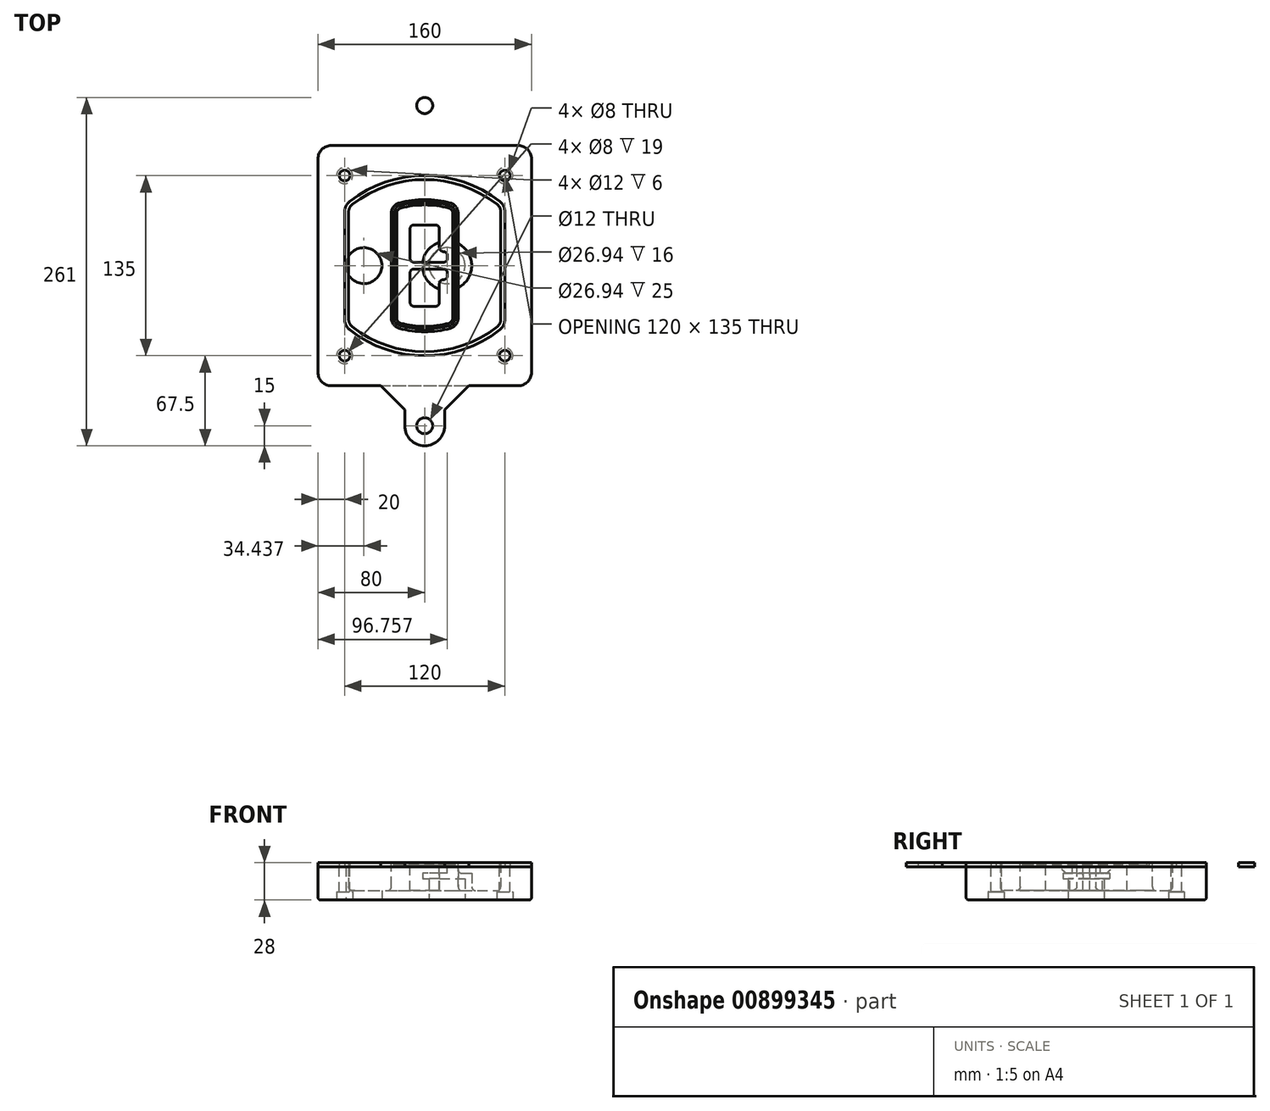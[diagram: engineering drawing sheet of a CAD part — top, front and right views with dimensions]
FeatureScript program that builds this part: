
annotation { "Feature Type Name" : "Feature", "Feature Type Description" : "" }
export const myFeature = defineFeature(function(context is Context, id is Id, definition is map)
    precondition{}
    {
        {
            var Q0;
            Q0=qCreatedBy(makeId("Top.planeOp"),FACE);
            var sketch = newSketch(context, id + "F0", { "sketchPlane" : qUnion([Q0])});
            skPoint(sketch, "E0.rect.middle", {"position": v(0, 0) * mm});
            skLineSegment(sketch, "E1.bottom", {"start": v(-70, -90) * mm, "end": v(70, -90) * mm});
            skLineSegment(sketch, "E1.top", {"start": v(-70, 90) * mm, "end": v(70, 90) * mm});
            skLineSegment(sketch, "E1.left", {"start": v(-80, -80) * mm, "end": v(-80, 80) * mm});
            skLineSegment(sketch, "E1.right", {"start": v(80, -80) * mm, "end": v(80, 80) * mm});
            skLineSegment(sketch, "E2", {"start": v(-80, 90) * mm, "end": v(80, -90) * mm, "construction": true});
            skLineSegment(sketch, "E3", {"start": v(80, 90) * mm, "end": v(-80, -90) * mm, "construction": true});
            skCircle(sketch, "E4", {"center": v(-60, 67.5) * mm, "radius": 4 * mm});
            skCircle(sketch, "E5", {"center": v(60, 67.5) * mm, "radius": 4 * mm});
            skCircle(sketch, "E6", {"center": v(60, -67.5) * mm, "radius": 4 * mm});
            skCircle(sketch, "E7", {"center": v(-60, -67.5) * mm, "radius": 4 * mm});
            skLineSegment(sketch, "E8", {"start": v(-60, 67.5) * mm, "end": v(60, 67.5) * mm, "construction": true});
            skLineSegment(sketch, "E9", {"start": v(60, 67.5) * mm, "end": v(60, -67.5) * mm, "construction": true});
            skLineSegment(sketch, "E10", {"start": v(60, -67.5) * mm, "end": v(-60, -67.5) * mm, "construction": true});
            skLineSegment(sketch, "E11", {"start": v(-60, -67.5) * mm, "end": v(-60, 67.5) * mm, "construction": true});
            skLineSegment(sketch, "E12", {"start": v(-60, 40.3) * mm, "end": v(-60, -40.3) * mm});
            skLineSegment(sketch, "E13", {"start": v(60, 40.3) * mm, "end": v(60, -40.3) * mm});
            skArc(sketch, "E14", {"start": v(56.15, 48.18) * mm, "mid": v(0, 67.5) * mm, "end": v(-56.15, 48.18) * mm});
            skArc(sketch, "E15", {"start": v(-56.15, -48.18) * mm, "mid": v(0, -67.5) * mm, "end": v(56.15, -48.18) * mm});
            skLineSegment(sketch, "E16", {"start": v(-60, 0) * mm, "end": v(60, 0) * mm, "construction": true});
            skPoint(sketch, "E17.visualSharp", {"position": v(-60, -45) * mm});
            skArc(sketch, "E17.filletArc", {"start": v(-60, -40.3) * mm, "mid": v(-58.99, -44.68) * mm, "end": v(-56.15, -48.18) * mm});
            skPoint(sketch, "E18.visualSharp", {"position": v(-60, 45) * mm});
            skArc(sketch, "E18.filletArc", {"start": v(-56.15, 48.18) * mm, "mid": v(-58.99, 44.68) * mm, "end": v(-60, 40.3) * mm});
            skPoint(sketch, "E19.visualSharp", {"position": v(60, 45) * mm});
            skArc(sketch, "E19.filletArc", {"start": v(60, 40.3) * mm, "mid": v(58.99, 44.68) * mm, "end": v(56.15, 48.18) * mm});
            skPoint(sketch, "E20.visualSharp", {"position": v(60, -45) * mm});
            skArc(sketch, "E20.filletArc", {"start": v(56.15, -48.18) * mm, "mid": v(58.99, -44.68) * mm, "end": v(60, -40.3) * mm});
            skPoint(sketch, "E21.visualSharp", {"position": v(-80, 90) * mm});
            skArc(sketch, "E21.filletArc", {"start": v(-70, 90) * mm, "mid": v(-77.07, 87.07) * mm, "end": v(-80, 80) * mm});
            skPoint(sketch, "E22.visualSharp", {"position": v(80, 90) * mm});
            skArc(sketch, "E22.filletArc", {"start": v(80, 80) * mm, "mid": v(77.07, 87.07) * mm, "end": v(70, 90) * mm});
            skPoint(sketch, "E23.visualSharp", {"position": v(80, -90) * mm});
            skArc(sketch, "E23.filletArc", {"start": v(70, -90) * mm, "mid": v(77.07, -87.07) * mm, "end": v(80, -80) * mm});
            skPoint(sketch, "E24.visualSharp", {"position": v(-80, -90) * mm});
            skArc(sketch, "E24.filletArc", {"start": v(-80, -80) * mm, "mid": v(-77.07, -87.07) * mm, "end": v(-70, -90) * mm});
            skArc(sketch, "E25.0", {"start": v(57, 40.3) * mm, "mid": v(56.3, 43.36) * mm, "end": v(54.3, 45.81) * mm});
            skLineSegment(sketch, "E25.1", {"start": v(57, 40.3) * mm, "end": v(57, -40.3) * mm});
            skArc(sketch, "E25.2", {"start": v(54.3, -45.81) * mm, "mid": v(56.3, -43.36) * mm, "end": v(57, -40.3) * mm});
            skArc(sketch, "E25.3", {"start": v(-54.3, -45.81) * mm, "mid": v(0, -64.5) * mm, "end": v(54.3, -45.81) * mm});
            skArc(sketch, "E25.4", {"start": v(-57, -40.3) * mm, "mid": v(-56.3, -43.36) * mm, "end": v(-54.3, -45.81) * mm});
            skArc(sketch, "E25.5", {"start": v(54.3, 45.81) * mm, "mid": v(0, 64.5) * mm, "end": v(-54.3, 45.81) * mm});
            skLineSegment(sketch, "E25.6", {"start": v(-57, 40.3) * mm, "end": v(-57, -40.3) * mm});
            skArc(sketch, "E25.7", {"start": v(-54.3, 45.81) * mm, "mid": v(-56.3, 43.36) * mm, "end": v(-57, 40.3) * mm});
            skArc(sketch, "E26.0", {"start": v(-58.62, 51.33) * mm, "mid": v(-62.58, 46.43) * mm, "end": v(-64, 40.3) * mm});
            skArc(sketch, "E26.1", {"start": v(58.62, 51.33) * mm, "mid": v(0, 71.5) * mm, "end": v(-58.62, 51.33) * mm});
            skArc(sketch, "E26.2", {"start": v(64, 40.3) * mm, "mid": v(62.58, 46.43) * mm, "end": v(58.62, 51.33) * mm});
            skLineSegment(sketch, "E26.3", {"start": v(64, 40.3) * mm, "end": v(64, -40.3) * mm});
            skArc(sketch, "E26.4", {"start": v(58.62, -51.33) * mm, "mid": v(62.58, -46.43) * mm, "end": v(64, -40.3) * mm});
            skLineSegment(sketch, "E26.5", {"start": v(-64, 40.3) * mm, "end": v(-64, -40.3) * mm});
            skArc(sketch, "E26.6", {"start": v(-58.62, -51.33) * mm, "mid": v(0, -71.5) * mm, "end": v(58.62, -51.33) * mm});
            skArc(sketch, "E26.7", {"start": v(-64, -40.3) * mm, "mid": v(-62.58, -46.43) * mm, "end": v(-58.62, -51.33) * mm});
            skSolve(sketch);
        }
        {
            var Q0;
            Q0=makeQuery(id+"F0.imprint","IMPRINT",FACE,{"disambiguationData":[TD([[makeQuery(id+"F0.imprint","IMPRINT",EDGE,{"derivedFrom":sQuery(id+"F0.wireOp",EDGE,"E1.bottom")}),1.0]])]});
            var Q1;
            Q1=makeQuery(id+"F0.imprint","IMPRINT",FACE,{"disambiguationData":[TD([[makeQuery(id+"F0.imprint","IMPRINT",EDGE,{"derivedFrom":sQuery(id+"F0.wireOp",EDGE,"E12")}),1.0]])]});
            var Q2;
            Q2=makeQuery(id+"F0.imprint","IMPRINT",FACE,{"disambiguationData":[TD([[makeQuery(id+"F0.imprint","IMPRINT",EDGE,{"derivedFrom":sQuery(id+"F0.wireOp",EDGE,"E25.0")}),1.0]])]});
            var Q3;
            Q3=makeQuery(id+"F0.imprint","IMPRINT",FACE,{"disambiguationData":[TD([[makeQuery(id+"F0.imprint","IMPRINT",EDGE,{"derivedFrom":sQuery(id+"F0.wireOp",EDGE,"E12")}),-1.0]])]});
            extrude(context, id + "F1", {"entities" : qUnion([Q0, Q1, Q2, Q3]), "oppositeDirection" : true, "depth" : 25 * mm});
        }
        {
            var Q0;
            Q0=makeQuery(id+"F0.imprint","IMPRINT",FACE,{"disambiguationData":[TD([[makeQuery(id+"F0.imprint","IMPRINT",EDGE,{"derivedFrom":sQuery(id+"F0.wireOp",EDGE,"E12")}),1.0]])]});
            extrude(context, id + "F2", {"entities" : qUnion([Q0]), "operationType" : NewBodyOperationType.ADD, "depth" : 3 * mm});
        }
        {
            var Q0;
            Q0=makeQuery(id+"F0.imprint","IMPRINT",FACE,{"disambiguationData":[TD([[makeQuery(id+"F0.imprint","IMPRINT",EDGE,{"derivedFrom":sQuery(id+"F0.wireOp",EDGE,"E25.0")}),1.0]])]});
            extrude(context, id + "F3", {"entities" : qUnion([Q0]), "operationType" : NewBodyOperationType.REMOVE, "oppositeDirection" : true, "depth" : 18 * mm});
        }
        {
            var Q0;
            Q0=makeQuery(id+"F2.opExtrude","CAP_FACE",FACE,{"disambiguationData":[OSD([sQuery(id+"F0.wireOp",EDGE,"E12"),sQuery(id+"F0.wireOp",EDGE,"E13"),sQuery(id+"F0.wireOp",EDGE,"E14"),sQuery(id+"F0.wireOp",EDGE,"E15"),sQuery(id+"F0.wireOp",EDGE,"E17.filletArc"),sQuery(id+"F0.wireOp",EDGE,"E18.filletArc"),sQuery(id+"F0.wireOp",EDGE,"E19.filletArc"),sQuery(id+"F0.wireOp",EDGE,"E20.filletArc"),sQuery(id+"F0.wireOp",EDGE,"E25.0"),sQuery(id+"F0.wireOp",EDGE,"E25.1"),sQuery(id+"F0.wireOp",EDGE,"E25.2"),sQuery(id+"F0.wireOp",EDGE,"E25.3"),sQuery(id+"F0.wireOp",EDGE,"E25.4"),sQuery(id+"F0.wireOp",EDGE,"E25.5"),sQuery(id+"F0.wireOp",EDGE,"E25.6"),sQuery(id+"F0.wireOp",EDGE,"E25.7")])],"isStart":false});
            var sketch = newSketch(context, id + "F4", { "sketchPlane" : qUnion([Q0])});
            skArc(sketch, "E27.0", {"start": v(-19.08, -46.97) * mm, "mid": v(0, -49.5) * mm, "end": v(19.08, -46.97) * mm});
            skArc(sketch, "E28.0", {"start": v(19.08, 46.97) * mm, "mid": v(0, 49.5) * mm, "end": v(-19.08, 46.97) * mm});
            skLineSegment(sketch, "E29", {"start": v(-25, 39.25) * mm, "end": v(-25, -39.25) * mm});
            skLineSegment(sketch, "E30", {"start": v(25, 39.25) * mm, "end": v(25, -39.25) * mm});
            skLineSegment(sketch, "E31", {"start": v(-25, 45.1) * mm, "end": v(25, 45.1) * mm, "construction": true});
            skLineSegment(sketch, "E32", {"start": v(-25, -45.1) * mm, "end": v(25, -45.1) * mm, "construction": true});
            skPoint(sketch, "E33.visualSharp", {"position": v(-25, 45.1) * mm});
            skArc(sketch, "E33.filletArc", {"start": v(-19.08, 46.97) * mm, "mid": v(-23.35, 44.11) * mm, "end": v(-25, 39.25) * mm});
            skPoint(sketch, "E34.visualSharp", {"position": v(25, 45.1) * mm});
            skArc(sketch, "E34.filletArc", {"start": v(25, 39.25) * mm, "mid": v(23.35, 44.11) * mm, "end": v(19.08, 46.97) * mm});
            skPoint(sketch, "E35.visualSharp", {"position": v(25, -45.1) * mm});
            skArc(sketch, "E35.filletArc", {"start": v(19.08, -46.97) * mm, "mid": v(23.35, -44.11) * mm, "end": v(25, -39.25) * mm});
            skPoint(sketch, "E36.visualSharp", {"position": v(-25, -45.1) * mm});
            skArc(sketch, "E36.filletArc", {"start": v(-25, -39.25) * mm, "mid": v(-23.35, -44.11) * mm, "end": v(-19.08, -46.97) * mm});
            skArc(sketch, "E37.0", {"start": v(54.3, 45.81) * mm, "mid": v(0, 64.5) * mm, "end": v(-54.3, 45.81) * mm});
            skArc(sketch, "E37.1", {"start": v(-54.3, 45.81) * mm, "mid": v(-56.3, 43.36) * mm, "end": v(-57, 40.3) * mm});
            skLineSegment(sketch, "E37.2", {"start": v(-57, 40.3) * mm, "end": v(-57, -40.3) * mm});
            skArc(sketch, "E37.3", {"start": v(-57, -40.3) * mm, "mid": v(-56.3, -43.36) * mm, "end": v(-54.3, -45.81) * mm});
            skArc(sketch, "E37.4", {"start": v(-54.3, -45.81) * mm, "mid": v(0, -64.5) * mm, "end": v(54.3, -45.81) * mm});
            skArc(sketch, "E37.5", {"start": v(54.3, -45.81) * mm, "mid": v(56.3, -43.36) * mm, "end": v(57, -40.3) * mm});
            skLineSegment(sketch, "E37.6", {"start": v(57, 40.3) * mm, "end": v(57, -40.3) * mm});
            skArc(sketch, "E37.7", {"start": v(57, 40.3) * mm, "mid": v(56.3, 43.36) * mm, "end": v(54.3, 45.81) * mm});
            skLineSegment(sketch, "E38.0", {"start": v(23, 39.25) * mm, "end": v(23, -39.25) * mm});
            skArc(sketch, "E38.1", {"start": v(18.56, -45.04) * mm, "mid": v(21.76, -42.9) * mm, "end": v(23, -39.25) * mm});
            skArc(sketch, "E38.2", {"start": v(-18.56, -45.04) * mm, "mid": v(0, -47.5) * mm, "end": v(18.56, -45.04) * mm});
            skArc(sketch, "E38.3", {"start": v(-23, -39.25) * mm, "mid": v(-21.76, -42.9) * mm, "end": v(-18.56, -45.04) * mm});
            skLineSegment(sketch, "E38.4", {"start": v(-23, 39.25) * mm, "end": v(-23, -39.25) * mm});
            skArc(sketch, "E38.5", {"start": v(23, 39.25) * mm, "mid": v(21.76, 42.9) * mm, "end": v(18.56, 45.04) * mm});
            skArc(sketch, "E38.6", {"start": v(-18.56, 45.04) * mm, "mid": v(-21.76, 42.9) * mm, "end": v(-23, 39.25) * mm});
            skArc(sketch, "E38.7", {"start": v(18.56, 45.04) * mm, "mid": v(0, 47.5) * mm, "end": v(-18.56, 45.04) * mm});
            skArc(sketch, "E39.0", {"start": v(21, 39.25) * mm, "mid": v(20.18, 41.68) * mm, "end": v(18.04, 43.1) * mm});
            skLineSegment(sketch, "E39.1", {"start": v(21, 39.25) * mm, "end": v(21, -39.25) * mm});
            skArc(sketch, "E39.2", {"start": v(18.04, -43.1) * mm, "mid": v(20.18, -41.68) * mm, "end": v(21, -39.25) * mm});
            skArc(sketch, "E39.3", {"start": v(-18.04, -43.1) * mm, "mid": v(0, -45.5) * mm, "end": v(18.04, -43.1) * mm});
            skArc(sketch, "E39.4", {"start": v(-21, -39.25) * mm, "mid": v(-20.18, -41.68) * mm, "end": v(-18.04, -43.1) * mm});
            skArc(sketch, "E39.5", {"start": v(18.04, 43.1) * mm, "mid": v(0, 45.5) * mm, "end": v(-18.04, 43.1) * mm});
            skLineSegment(sketch, "E39.6", {"start": v(-21, 39.25) * mm, "end": v(-21, -39.25) * mm});
            skArc(sketch, "E39.7", {"start": v(-18.04, 43.1) * mm, "mid": v(-20.18, 41.68) * mm, "end": v(-21, 39.25) * mm});
            skLineSegment(sketch, "E40", {"start": v(-25, 0) * mm, "end": v(25, 0) * mm, "construction": true});
            skLineSegment(sketch, "E41", {"start": v(-11, 5.5) * mm, "end": v(-11, 27.5) * mm});
            skLineSegment(sketch, "E42", {"start": v(-8, 30.5) * mm, "end": v(8, 30.5) * mm});
            skLineSegment(sketch, "E43", {"start": v(11, 27.5) * mm, "end": v(11, 13.5) * mm});
            skLineSegment(sketch, "E44", {"start": v(14, 10.5) * mm, "end": v(14, 10.5) * mm});
            skLineSegment(sketch, "E45", {"start": v(17, 7.5) * mm, "end": v(17, 5.5) * mm});
            skLineSegment(sketch, "E46", {"start": v(14, 2.5) * mm, "end": v(-8, 2.5) * mm});
            skPoint(sketch, "E47.visualSharp", {"position": v(-11, 30.5) * mm});
            skArc(sketch, "E47.filletArc", {"start": v(-8, 30.5) * mm, "mid": v(-10.12, 29.62) * mm, "end": v(-11, 27.5) * mm});
            skPoint(sketch, "E48.visualSharp", {"position": v(11, 30.5) * mm});
            skArc(sketch, "E48.filletArc", {"start": v(11, 27.5) * mm, "mid": v(10.12, 29.62) * mm, "end": v(8, 30.5) * mm});
            skPoint(sketch, "E49.visualSharp", {"position": v(11, 10.5) * mm});
            skArc(sketch, "E49.filletArc", {"start": v(11, 13.5) * mm, "mid": v(11.88, 11.38) * mm, "end": v(14, 10.5) * mm});
            skPoint(sketch, "E50.visualSharp", {"position": v(17, 10.5) * mm});
            skArc(sketch, "E50.filletArc", {"start": v(17, 7.5) * mm, "mid": v(16.12, 9.62) * mm, "end": v(14, 10.5) * mm});
            skPoint(sketch, "E51.visualSharp", {"position": v(17, 2.5) * mm});
            skArc(sketch, "E51.filletArc", {"start": v(14, 2.5) * mm, "mid": v(16.12, 3.38) * mm, "end": v(17, 5.5) * mm});
            skPoint(sketch, "E52.visualSharp", {"position": v(-11, 2.5) * mm});
            skArc(sketch, "E52.filletArc", {"start": v(-11, 5.5) * mm, "mid": v(-10.12, 3.38) * mm, "end": v(-8, 2.5) * mm});
            skLineSegment(sketch, "E53.0.MirrorCS", {"start": v(14, -2.5) * mm, "end": v(-8, -2.5) * mm});
            skArc(sketch, "E54.0.MirrorCS", {"start": v(-11, -5.5) * mm, "mid": v(-10.12, -3.38) * mm, "end": v(-8, -2.5) * mm});
            skLineSegment(sketch, "E55.0.MirrorCS", {"start": v(-11, -5.5) * mm, "end": v(-11, -27.5) * mm});
            skArc(sketch, "E56.0.MirrorCS", {"start": v(-8, -30.5) * mm, "mid": v(-10.12, -29.62) * mm, "end": v(-11, -27.5) * mm});
            skLineSegment(sketch, "E57.0.MirrorCS", {"start": v(-8, -30.5) * mm, "end": v(8, -30.5) * mm});
            skArc(sketch, "E58.0.MirrorCS", {"start": v(11, -27.5) * mm, "mid": v(10.12, -29.62) * mm, "end": v(8, -30.5) * mm});
            skLineSegment(sketch, "E59.0.MirrorCS", {"start": v(11, -27.5) * mm, "end": v(11, -13.5) * mm});
            skArc(sketch, "E60.0.MirrorCS", {"start": v(11, -13.5) * mm, "mid": v(11.88, -11.38) * mm, "end": v(14, -10.5) * mm});
            skArc(sketch, "E61.0.MirrorCS", {"start": v(17, -7.5) * mm, "mid": v(16.12, -9.62) * mm, "end": v(14, -10.5) * mm});
            skLineSegment(sketch, "E62.0.MirrorCS", {"start": v(17, -7.5) * mm, "end": v(17, -5.5) * mm});
            skArc(sketch, "E63.0.MirrorCS", {"start": v(14, -2.5) * mm, "mid": v(16.12, -3.38) * mm, "end": v(17, -5.5) * mm});
            skSolve(sketch);
        }
        {
            var Q0;
            Q0=makeQuery(id+"F4.imprint","IMPRINT",FACE,{"disambiguationData":[TD([[makeQuery(id+"F4.imprint","IMPRINT",EDGE,{"derivedFrom":sQuery(id+"F4.wireOp",EDGE,"E27.0")}),1.0]])]});
            var Q1;
            Q1=makeQuery(id+"F4.imprint","IMPRINT",FACE,{"disambiguationData":[TD([[makeQuery(id+"F4.imprint","IMPRINT",EDGE,{"derivedFrom":sQuery(id+"F4.wireOp",EDGE,"E38.0")}),-1.0]])]});
            var Q2;
            Q2=makeQuery(id+"F4.imprint","IMPRINT",FACE,{"disambiguationData":[TD([[makeQuery(id+"F4.imprint","IMPRINT",EDGE,{"derivedFrom":sQuery(id+"F4.wireOp",EDGE,"E39.0")}),1.0]])]});
            extrude(context, id + "F5", {"entities" : qUnion([Q0, Q1, Q2]), "operationType" : NewBodyOperationType.ADD, "endBound" : BoundingType.UP_TO_NEXT, "oppositeDirection" : true, "depth" : 25 * mm});
        }
        {
            var Q0;
            Q0=makeQuery(id+"F4.imprint","IMPRINT",FACE,{"disambiguationData":[TD([[makeQuery(id+"F4.imprint","IMPRINT",EDGE,{"derivedFrom":sQuery(id+"F4.wireOp",EDGE,"E38.0")}),-1.0]])]});
            extrude(context, id + "F6", {"entities" : qUnion([Q0]), "operationType" : NewBodyOperationType.REMOVE, "oppositeDirection" : true, "depth" : 2 * mm});
        }
        {
            var Q0;
            Q0=makeQuery(id+"F1.opExtrude","CAP_FACE",FACE,{"disambiguationData":[OSD([sQuery(id+"F0.wireOp",EDGE,"E1.bottom"),sQuery(id+"F0.wireOp",EDGE,"E1.top"),sQuery(id+"F0.wireOp",EDGE,"E1.left"),sQuery(id+"F0.wireOp",EDGE,"E1.right"),sQuery(id+"F0.wireOp",EDGE,"E4"),sQuery(id+"F0.wireOp",EDGE,"E5"),sQuery(id+"F0.wireOp",EDGE,"E6"),sQuery(id+"F0.wireOp",EDGE,"E7"),sQuery(id+"F0.wireOp",EDGE,"E21.filletArc"),sQuery(id+"F0.wireOp",EDGE,"E22.filletArc"),sQuery(id+"F0.wireOp",EDGE,"E23.filletArc"),sQuery(id+"F0.wireOp",EDGE,"E24.filletArc")])],"isStart":false});
            var sketch = newSketch(context, id + "F7", { "sketchPlane" : qUnion([Q0])});
            skCircle(sketch, "E64", {"center": v(16.76, 0) * mm, "radius": 13.47 * mm});
            skCircle(sketch, "E65", {"center": v(-45.56, 0) * mm, "radius": 13.47 * mm});
            skLineSegment(sketch, "E66", {"start": v(80, 0) * mm, "end": v(-80, 0) * mm});
            skCircle(sketch, "E67", {"center": v(16.76, 0) * mm, "radius": 18.47 * mm});
            skCircle(sketch, "E68", {"center": v(60, -67.5) * mm, "radius": 6 * mm});
            skCircle(sketch, "E69", {"center": v(-60, -67.5) * mm, "radius": 6 * mm});
            skCircle(sketch, "E70", {"center": v(-60, 67.5) * mm, "radius": 6 * mm});
            skCircle(sketch, "E71", {"center": v(60, 67.5) * mm, "radius": 6 * mm});
            skSolve(sketch);
        }
        {
            var Q0;
            {var subQ1=sQuery(id+"F7.wireOp",EDGE,"E66");var subQ4=sQuery(id+"F7.wireOp",EDGE,"E64");var subQ6=makeQuery(id+"F7.imprint","INTERSECT",VERTEX,{"disambiguationData":[OD(0.0)],"derivedFrom":[subQ4,subQ1]});Q0=makeQuery(id+"F7.imprint","IMPRINT",FACE,{"disambiguationData":[TD([[makeQuery(id+"F7.imprint","IMPRINT",EDGE,{"disambiguationData":[TD([[subQ6,-1.0]])],"derivedFrom":subQ4}),-1.0]])]});}
            var Q1;
            {var subQ0=sQuery(id+"F7.wireOp",EDGE,"E66");var subQ1=sQuery(id+"F7.wireOp",EDGE,"E64");var subQ3=makeQuery(id+"F7.imprint","INTERSECT",VERTEX,{"disambiguationData":[OD(0.0)],"derivedFrom":[subQ1,subQ0]});Q1=makeQuery(id+"F7.imprint","IMPRINT",FACE,{"disambiguationData":[TD([[makeQuery(id+"F7.imprint","IMPRINT",EDGE,{"disambiguationData":[TD([[subQ3,-1.0]])],"derivedFrom":subQ1}),1.0]])]});}
            var Q2;
            {var subQ0=sQuery(id+"F7.wireOp",EDGE,"E66");var subQ1=sQuery(id+"F7.wireOp",EDGE,"E64");var subQ3=makeQuery(id+"F7.imprint","INTERSECT",VERTEX,{"disambiguationData":[OD(0.0)],"derivedFrom":[subQ1,subQ0]});Q2=makeQuery(id+"F7.imprint","IMPRINT",FACE,{"disambiguationData":[TD([[makeQuery(id+"F7.imprint","IMPRINT",EDGE,{"disambiguationData":[TD([[subQ3,1.0]])],"derivedFrom":subQ1}),1.0]])]});}
            var Q3;
            {var subQ1=sQuery(id+"F7.wireOp",EDGE,"E66");var subQ4=sQuery(id+"F7.wireOp",EDGE,"E64");var subQ6=makeQuery(id+"F7.imprint","INTERSECT",VERTEX,{"disambiguationData":[OD(0.0)],"derivedFrom":[subQ4,subQ1]});Q3=makeQuery(id+"F7.imprint","IMPRINT",FACE,{"disambiguationData":[TD([[makeQuery(id+"F7.imprint","IMPRINT",EDGE,{"disambiguationData":[TD([[subQ6,1.0]])],"derivedFrom":subQ4}),-1.0]])]});}
            extrude(context, id + "F8", {"entities" : qUnion([Q0, Q1, Q2, Q3]), "operationType" : NewBodyOperationType.ADD, "oppositeDirection" : true, "depth" : 20 * mm});
        }
        {
            var Q0;
            {var subQ0=sQuery(id+"F7.wireOp",EDGE,"E66");var subQ1=sQuery(id+"F7.wireOp",EDGE,"E64");var subQ3=makeQuery(id+"F7.imprint","INTERSECT",VERTEX,{"disambiguationData":[OD(0.0)],"derivedFrom":[subQ1,subQ0]});Q0=makeQuery(id+"F7.imprint","IMPRINT",FACE,{"disambiguationData":[TD([[makeQuery(id+"F7.imprint","IMPRINT",EDGE,{"disambiguationData":[TD([[subQ3,-1.0]])],"derivedFrom":subQ1}),1.0]])]});}
            var Q1;
            {var subQ0=sQuery(id+"F7.wireOp",EDGE,"E66");var subQ1=sQuery(id+"F7.wireOp",EDGE,"E64");var subQ3=makeQuery(id+"F7.imprint","INTERSECT",VERTEX,{"disambiguationData":[OD(0.0)],"derivedFrom":[subQ1,subQ0]});Q1=makeQuery(id+"F7.imprint","IMPRINT",FACE,{"disambiguationData":[TD([[makeQuery(id+"F7.imprint","IMPRINT",EDGE,{"disambiguationData":[TD([[subQ3,1.0]])],"derivedFrom":subQ1}),1.0]])]});}
            extrude(context, id + "F9", {"entities" : qUnion([Q0, Q1]), "operationType" : NewBodyOperationType.REMOVE, "oppositeDirection" : true, "depth" : 16 * mm});
        }
        {
            var Q0;
            {var subQ0=sQuery(id+"F7.wireOp",EDGE,"E66");var subQ1=sQuery(id+"F7.wireOp",EDGE,"E65");var subQ3=makeQuery(id+"F7.imprint","INTERSECT",VERTEX,{"disambiguationData":[OD(0.0)],"derivedFrom":[subQ1,subQ0]});Q0=makeQuery(id+"F7.imprint","IMPRINT",FACE,{"disambiguationData":[TD([[makeQuery(id+"F7.imprint","IMPRINT",EDGE,{"disambiguationData":[TD([[subQ3,-1.0]])],"derivedFrom":subQ1}),1.0]])]});}
            var Q1;
            {var subQ0=sQuery(id+"F7.wireOp",EDGE,"E66");var subQ1=sQuery(id+"F7.wireOp",EDGE,"E65");var subQ3=makeQuery(id+"F7.imprint","INTERSECT",VERTEX,{"disambiguationData":[OD(0.0)],"derivedFrom":[subQ1,subQ0]});Q1=makeQuery(id+"F7.imprint","IMPRINT",FACE,{"disambiguationData":[TD([[makeQuery(id+"F7.imprint","IMPRINT",EDGE,{"disambiguationData":[TD([[subQ3,1.0]])],"derivedFrom":subQ1}),1.0]])]});}
            extrude(context, id + "F10", {"entities" : qUnion([Q0, Q1]), "operationType" : NewBodyOperationType.REMOVE, "oppositeDirection" : true, "depth" : 25 * mm});
        }
        {
            var Q0;
            Q0=makeQuery(id+"F7.imprint","IMPRINT",FACE,{"disambiguationData":[TD([[makeQuery(id+"F7.imprint","IMPRINT",EDGE,{"derivedFrom":sQuery(id+"F7.wireOp",EDGE,"E68")}),1.0]])]});
            var Q1;
            Q1=makeQuery(id+"F7.imprint","IMPRINT",FACE,{"disambiguationData":[TD([[makeQuery(id+"F7.imprint","IMPRINT",EDGE,{"derivedFrom":makeQuery(id+"F1.opExtrude","CAP_EDGE",EDGE,{"disambiguationData":[OSD([sQuery(id+"F0.wireOp",EDGE,"E5")])],"isStart":false})}),-1.0]])]});
            var Q2;
            Q2=makeQuery(id+"F7.imprint","IMPRINT",FACE,{"disambiguationData":[TD([[makeQuery(id+"F7.imprint","IMPRINT",EDGE,{"derivedFrom":sQuery(id+"F7.wireOp",EDGE,"E69")}),1.0]])]});
            var Q3;
            Q3=makeQuery(id+"F7.imprint","IMPRINT",FACE,{"disambiguationData":[TD([[makeQuery(id+"F7.imprint","IMPRINT",EDGE,{"derivedFrom":makeQuery(id+"F1.opExtrude","CAP_EDGE",EDGE,{"disambiguationData":[OSD([sQuery(id+"F0.wireOp",EDGE,"E4")])],"isStart":false})}),-1.0]])]});
            var Q4;
            Q4=makeQuery(id+"F7.imprint","IMPRINT",FACE,{"disambiguationData":[TD([[makeQuery(id+"F7.imprint","IMPRINT",EDGE,{"derivedFrom":sQuery(id+"F7.wireOp",EDGE,"E70")}),1.0]])]});
            var Q5;
            Q5=makeQuery(id+"F7.imprint","IMPRINT",FACE,{"disambiguationData":[TD([[makeQuery(id+"F7.imprint","IMPRINT",EDGE,{"derivedFrom":makeQuery(id+"F1.opExtrude","CAP_EDGE",EDGE,{"disambiguationData":[OSD([sQuery(id+"F0.wireOp",EDGE,"E7")])],"isStart":false})}),-1.0]])]});
            var Q6;
            Q6=makeQuery(id+"F7.imprint","IMPRINT",FACE,{"disambiguationData":[TD([[makeQuery(id+"F7.imprint","IMPRINT",EDGE,{"derivedFrom":sQuery(id+"F7.wireOp",EDGE,"E71")}),1.0]])]});
            var Q7;
            Q7=makeQuery(id+"F7.imprint","IMPRINT",FACE,{"disambiguationData":[TD([[makeQuery(id+"F7.imprint","IMPRINT",EDGE,{"derivedFrom":makeQuery(id+"F1.opExtrude","CAP_EDGE",EDGE,{"disambiguationData":[OSD([sQuery(id+"F0.wireOp",EDGE,"E6")])],"isStart":false})}),-1.0]])]});
            extrude(context, id + "F11", {"entities" : qUnion([Q0, Q1, Q2, Q3, Q4, Q5, Q6, Q7]), "operationType" : NewBodyOperationType.REMOVE, "oppositeDirection" : true, "depth" : 6 * mm});
        }
        {
            var Q0;
            Q0=makeQuery(id+"F9.boolean.opBoolean","COPY",FACE,{"derivedFrom":makeQuery(id+"F9.opExtrude","CAP_FACE",FACE,{"disambiguationData":[OSD([sQuery(id+"F7.wireOp",EDGE,"E64")])],"isStart":false})});
            var sketch = newSketch(context, id + "F12", { "sketchPlane" : qUnion([Q0])});
            skArc(sketch, "E72.0", {"start": v(11, 17.55) * mm, "mid": v(2.57, 11.82) * mm, "end": v(-1.54, 2.5) * mm});
            skArc(sketch, "E72.1", {"start": v(-1.54, -2.5) * mm, "mid": v(2.57, -11.82) * mm, "end": v(11, -17.55) * mm});
            skLineSegment(sketch, "E73", {"start": v(-1.54, -2.5) * mm, "end": v(14, -2.5) * mm});
            skLineSegment(sketch, "E74.0", {"start": v(14, 2.5) * mm, "end": v(-1.54, 2.5) * mm});
            skArc(sketch, "E74.1", {"start": v(14, 2.5) * mm, "mid": v(16.12, 3.38) * mm, "end": v(17, 5.5) * mm});
            skLineSegment(sketch, "E74.2", {"start": v(17, 7.5) * mm, "end": v(17, 5.5) * mm});
            skArc(sketch, "E74.3", {"start": v(17, 7.5) * mm, "mid": v(16.12, 9.62) * mm, "end": v(14, 10.5) * mm});
            skArc(sketch, "E74.4", {"start": v(11, 13.5) * mm, "mid": v(11.88, 11.38) * mm, "end": v(14, 10.5) * mm});
            skLineSegment(sketch, "E74.5", {"start": v(11, 17.55) * mm, "end": v(11, 13.5) * mm});
            skLineSegment(sketch, "E74.7", {"start": v(14, -2.5) * mm, "end": v(-1.54, -2.5) * mm});
            skArc(sketch, "E74.8", {"start": v(14, -2.5) * mm, "mid": v(16.12, -3.38) * mm, "end": v(17, -5.5) * mm});
            skLineSegment(sketch, "E74.9", {"start": v(17, -7.5) * mm, "end": v(17, -5.5) * mm});
            skArc(sketch, "E74.10", {"start": v(17, -7.5) * mm, "mid": v(16.12, -9.62) * mm, "end": v(14, -10.5) * mm});
            skArc(sketch, "E74.11", {"start": v(11, -13.5) * mm, "mid": v(11.88, -11.38) * mm, "end": v(14, -10.5) * mm});
            skLineSegment(sketch, "E74.12", {"start": v(11, -17.55) * mm, "end": v(11, -13.5) * mm});
            skPoint(sketch, "E75.orphan", {"position": v(11, -27.5) * mm});
            skPoint(sketch, "E76.orphan", {"position": v(-8, -2.5) * mm});
            skPoint(sketch, "E77.orphan", {"position": v(-8, 2.5) * mm});
            skPoint(sketch, "E78.orphan", {"position": v(11, 27.5) * mm});
            skSolve(sketch);
        }
        {
            var Q0;
            {var subQ7=sQuery(id+"F12.wireOp",EDGE,"E72.0");var subQ14=sQuery(id+"F12.wireOp",EDGE,"E72.1");var subQ16=sQuery(id+"F12.wireOp",EDGE,"E74.1");var subQ18=sQuery(id+"F12.wireOp",EDGE,"E74.8");Q0=qUnion([makeQuery(id+"F12.imprint","IMPRINT",FACE,{"disambiguationData":[TD([[makeQuery(id+"F12.imprint","IMPRINT",EDGE,{"derivedFrom":subQ7}),1.0]])]}),makeQuery(id+"F12.imprint","IMPRINT",FACE,{"disambiguationData":[TD([[makeQuery(id+"F12.imprint","IMPRINT",EDGE,{"derivedFrom":subQ14}),1.0]])]}),makeQuery(id+"F12.imprint","IMPRINT",FACE,{"disambiguationData":[TD([[makeQuery(id+"F12.imprint","IMPRINT",EDGE,{"derivedFrom":subQ16}),1.0]])]}),makeQuery(id+"F12.imprint","IMPRINT",FACE,{"disambiguationData":[TD([[makeQuery(id+"F12.imprint","IMPRINT",EDGE,{"derivedFrom":subQ18}),-1.0]])]})]);}
            var Q1;
            Q1=makeQuery(id+"F5.boolean.opBoolean","SPLIT",FACE,{"disambiguationData":[TD([makeQuery(id+"F5.opExtrude","SWEPT_FACE",FACE,{"disambiguationData":[OSD([sQuery(id+"F4.wireOp",EDGE,"E41")])]})])],"derivedFrom":makeQuery(id+"F3.boolean.opBoolean","COPY",FACE,{"derivedFrom":makeQuery(id+"F3.opExtrude","CAP_FACE",FACE,{"disambiguationData":[OSD([sQuery(id+"F0.wireOp",EDGE,"E25.0"),sQuery(id+"F0.wireOp",EDGE,"E25.1"),sQuery(id+"F0.wireOp",EDGE,"E25.2"),sQuery(id+"F0.wireOp",EDGE,"E25.3"),sQuery(id+"F0.wireOp",EDGE,"E25.4"),sQuery(id+"F0.wireOp",EDGE,"E25.5"),sQuery(id+"F0.wireOp",EDGE,"E25.6"),sQuery(id+"F0.wireOp",EDGE,"E25.7")])],"isStart":false})})});
            extrude(context, id + "F13", {"entities" : qUnion([Q0]), "operationType" : NewBodyOperationType.REMOVE, "endBound" : BoundingType.UP_TO_SURFACE, "endBoundEntityFace" : qUnion([Q1]), "depth" : 25 * mm});
        }
        {
            var Q0;
            Q0=makeQuery(id+"F3.boolean.opBoolean","COPY",EDGE,{"derivedFrom":makeQuery(id+"F3.opExtrude","CAP_EDGE",EDGE,{"disambiguationData":[OSD([sQuery(id+"F0.wireOp",EDGE,"E25.6")])],"isStart":false})});
            var Q1;
            Q1=makeQuery(id+"F8.boolean.opBoolean","INTERSECT",EDGE,{"derivedFrom":[makeQuery(id+"F5.opExtrude","SWEPT_FACE",FACE,{"disambiguationData":[OSD([sQuery(id+"F4.wireOp",EDGE,"E30")])]}),makeQuery(id+"F8.opExtrude","CAP_FACE",FACE,{"disambiguationData":[OSD([sQuery(id+"F7.wireOp",EDGE,"E67")])],"isStart":false})]});
            var Q2;
            Q2=makeQuery(id+"F8.boolean.opBoolean","INTERSECT",EDGE,{"disambiguationData":[OD(1.0)],"derivedFrom":[makeQuery(id+"F5.opExtrude","SWEPT_FACE",FACE,{"disambiguationData":[OSD([sQuery(id+"F4.wireOp",EDGE,"E30")])]}),makeQuery(id+"F8.opExtrude","SWEPT_FACE",FACE,{"disambiguationData":[OSD([sQuery(id+"F7.wireOp",EDGE,"E67")])]})]});
            var Q3;
            {var subQ0=sQuery(id+"F4.wireOp",EDGE,"E30");Q3=makeQuery(id+"F8.boolean.opBoolean","SPLIT",EDGE,{"disambiguationData":[TD([makeQuery(id+"F5.opExtrude","SWEPT_FACE",FACE,{"disambiguationData":[OSD([sQuery(id+"F4.wireOp",EDGE,"E35.filletArc")])]})])],"derivedFrom":makeQuery(id+"F5.opExtrude","CAP_EDGE",EDGE,{"disambiguationData":[OSD([subQ0])],"isStart":false})});}
            var Q4;
            {var subQ0=sQuery(id+"F0.wireOp",EDGE,"E25.7");var subQ1=sQuery(id+"F0.wireOp",EDGE,"E25.1");var subQ2=sQuery(id+"F0.wireOp",EDGE,"E25.6");var subQ3=sQuery(id+"F0.wireOp",EDGE,"E25.5");var subQ4=sQuery(id+"F0.wireOp",EDGE,"E25.4");var subQ5=sQuery(id+"F0.wireOp",EDGE,"E25.0");var subQ6=sQuery(id+"F0.wireOp",EDGE,"E25.2");var subQ7=sQuery(id+"F0.wireOp",EDGE,"E25.3");Q4=makeQuery(id+"F8.boolean.opBoolean","INTERSECT",EDGE,{"derivedFrom":[makeQuery(id+"F5.boolean.opBoolean","SPLIT",FACE,{"disambiguationData":[TD([makeQuery(id+"F2.opExtrude","SWEPT_FACE",FACE,{"disambiguationData":[OSD([subQ5])]})])],"derivedFrom":makeQuery(id+"F3.boolean.opBoolean","COPY",FACE,{"derivedFrom":makeQuery(id+"F3.opExtrude","CAP_FACE",FACE,{"disambiguationData":[OSD([subQ5,subQ1,subQ6,subQ7,subQ4,subQ3,subQ2,subQ0])],"isStart":false})})}),makeQuery(id+"F8.opExtrude","SWEPT_FACE",FACE,{"disambiguationData":[OSD([sQuery(id+"F7.wireOp",EDGE,"E67")])]})]});}
            var Q5;
            Q5=makeQuery(id+"F8.boolean.opBoolean","INTERSECT",EDGE,{"disambiguationData":[OD(0.0)],"derivedFrom":[makeQuery(id+"F5.opExtrude","SWEPT_FACE",FACE,{"disambiguationData":[OSD([sQuery(id+"F4.wireOp",EDGE,"E30")])]}),makeQuery(id+"F8.opExtrude","SWEPT_FACE",FACE,{"disambiguationData":[OSD([sQuery(id+"F7.wireOp",EDGE,"E67")])]})]});
            fillet(context, id + "F14", {"entities" : qUnion([Q0, Q1, Q2, Q3, Q4, Q5]), "radius" : 3 * mm, "tangentPropagation" : true, "allowEdgeOverflow" : false});
        }
        {
            var Q0;
            Q0=makeQuery(id+"F1.opExtrude","CAP_EDGE",EDGE,{"disambiguationData":[OSD([sQuery(id+"F0.wireOp",EDGE,"E1.bottom")])],"isStart":false});
            fillet(context, id + "F15", {"entities" : qUnion([Q0]), "radius" : 2 * mm, "tangentPropagation" : true, "allowEdgeOverflow" : false});
        }
        {
            var Q0;
            {var subQ0=sQuery(id+"F0.wireOp",EDGE,"E21.filletArc");var subQ1=sQuery(id+"F0.wireOp",EDGE,"E7");var subQ2=sQuery(id+"F0.wireOp",EDGE,"E6");var subQ3=sQuery(id+"F0.wireOp",EDGE,"E5");var subQ4=sQuery(id+"F0.wireOp",EDGE,"E4");var subQ5=sQuery(id+"F0.wireOp",EDGE,"E22.filletArc");var subQ6=sQuery(id+"F0.wireOp",EDGE,"E1.bottom");var subQ7=sQuery(id+"F0.wireOp",EDGE,"E1.right");var subQ8=sQuery(id+"F0.wireOp",EDGE,"E1.top");var subQ9=sQuery(id+"F0.wireOp",EDGE,"E1.left");var subQ10=sQuery(id+"F0.wireOp",EDGE,"E23.filletArc");var subQ11=sQuery(id+"F0.wireOp",EDGE,"E24.filletArc");Q0=makeQuery(id+"F2.boolean.opBoolean","SPLIT",FACE,{"disambiguationData":[TD([makeQuery(id+"F1.opExtrude","SWEPT_FACE",FACE,{"disambiguationData":[OSD([subQ6])]})])],"derivedFrom":makeQuery(id+"F1.opExtrude","CAP_FACE",FACE,{"disambiguationData":[OSD([subQ6,subQ8,subQ9,subQ7,subQ4,subQ3,subQ2,subQ1,subQ0,subQ5,subQ10,subQ11])],"isStart":true})});}
            var sketch = newSketch(context, id + "F16", { "sketchPlane" : qUnion([Q0])});
            skLineSegment(sketch, "E79", {"start": v(0, 90) * mm, "end": v(0, 120) * mm, "construction": true});
            skCircle(sketch, "E80", {"center": v(0, 120) * mm, "radius": 6 * mm});
            skLineSegment(sketch, "E81", {"start": v(-33, 90) * mm, "end": v(-15, 108) * mm});
            skLineSegment(sketch, "E82", {"start": v(-15, 108) * mm, "end": v(-15, 120) * mm});
            skLineSegment(sketch, "E83", {"start": v(15, 120) * mm, "end": v(15, 108) * mm});
            skLineSegment(sketch, "E84", {"start": v(15, 108) * mm, "end": v(33, 90) * mm});
            skArc(sketch, "E85", {"start": v(15, 120) * mm, "mid": v(0, 135) * mm, "end": v(-15, 120) * mm});
            skLineSegment(sketch, "E86", {"start": v(-74.99, 0) * mm, "end": v(80, 0) * mm, "construction": true});
            skLineSegment(sketch, "E87.MirrorCS", {"start": v(15, 108) * mm, "end": v(15, 120) * mm});
            skLineSegment(sketch, "E88.MirrorCS", {"start": v(-15, 108) * mm, "end": v(-33, 90) * mm});
            skLineSegment(sketch, "E89.MirrorCS", {"start": v(-15, 120) * mm, "end": v(-15, 108) * mm});
            skLineSegment(sketch, "E90.MirrorCS", {"start": v(33, 90) * mm, "end": v(15, 108) * mm});
            skArc(sketch, "E91.MirrorCS", {"start": v(-15, 120) * mm, "mid": v(0, 135) * mm, "end": v(15, 120) * mm});
            skLineSegment(sketch, "E92.MirrorCS", {"start": v(74.99, 0) * mm, "end": v(-80, 0) * mm, "construction": true});
            skArc(sketch, "E93.MirrorCS", {"start": v(15, -120) * mm, "mid": v(0, -135) * mm, "end": v(-15, -120) * mm});
            skLineSegment(sketch, "E94.MirrorCS", {"start": v(-15, -108) * mm, "end": v(-33, -90) * mm});
            skLineSegment(sketch, "E95.MirrorCS", {"start": v(33, -90) * mm, "end": v(15, -108) * mm});
            skLineSegment(sketch, "E96.MirrorCS", {"start": v(-15, -108) * mm, "end": v(-15, -120) * mm});
            skLineSegment(sketch, "E97.MirrorCS", {"start": v(15, -120) * mm, "end": v(15, -108) * mm});
            skLineSegment(sketch, "E98.MirrorCS", {"start": v(15, -108) * mm, "end": v(33, -90) * mm});
            skCircle(sketch, "E99.MirrorC", {"center": v(0, -120) * mm, "radius": 6 * mm});
            skLineSegment(sketch, "E100.MirrorCS", {"start": v(-33, -90) * mm, "end": v(-15, -108) * mm});
            skLineSegment(sketch, "E101.MirrorCS", {"start": v(-15, -120) * mm, "end": v(-15, -108) * mm});
            skArc(sketch, "E102.MirrorCS", {"start": v(-15, -120) * mm, "mid": v(0, -135) * mm, "end": v(15, -120) * mm});
            skLineSegment(sketch, "E103.MirrorCS", {"start": v(15, -108) * mm, "end": v(15, -120) * mm});
            skLineSegment(sketch, "E104.MirrorCS", {"start": v(0, -90) * mm, "end": v(0, -120) * mm, "construction": true});
            skSolve(sketch);
        }
        {
            var Q0;
            {var subQ1=sQuery(id+"F16.wireOp",EDGE,"E94.MirrorCS");Q0=makeQuery(id+"F16.imprint","IMPRINT",FACE,{"disambiguationData":[TD([[makeQuery(id+"F16.imprint","IMPRINT",EDGE,{"derivedFrom":subQ1}),-1.0]])]});}
            var Q1;
            Q1=makeQuery(id+"F16.imprint","IMPRINT",FACE,{"disambiguationData":[TD([[makeQuery(id+"F16.imprint","IMPRINT",EDGE,{"derivedFrom":sQuery(id+"F16.wireOp",EDGE,"E80")}),1.0]])]});
            var Q2;
            Q2=makeQuery(id+"F16.imprint","IMPRINT",FACE,{"disambiguationData":[TD([[makeQuery(id+"F16.imprint","IMPRINT",EDGE,{"derivedFrom":makeQuery(id+"F1.opExtrude","CAP_EDGE",EDGE,{"disambiguationData":[OSD([sQuery(id+"F0.wireOp",EDGE,"E1.left")])],"isStart":true})}),-1.0]])]});
            var Q3;
            Q3=makeQuery(id+"F2.opExtrude","CAP_FACE",FACE,{"disambiguationData":[OSD([sQuery(id+"F0.wireOp",EDGE,"E12"),sQuery(id+"F0.wireOp",EDGE,"E13"),sQuery(id+"F0.wireOp",EDGE,"E14"),sQuery(id+"F0.wireOp",EDGE,"E15"),sQuery(id+"F0.wireOp",EDGE,"E17.filletArc"),sQuery(id+"F0.wireOp",EDGE,"E18.filletArc"),sQuery(id+"F0.wireOp",EDGE,"E19.filletArc"),sQuery(id+"F0.wireOp",EDGE,"E20.filletArc"),sQuery(id+"F0.wireOp",EDGE,"E25.0"),sQuery(id+"F0.wireOp",EDGE,"E25.1"),sQuery(id+"F0.wireOp",EDGE,"E25.2"),sQuery(id+"F0.wireOp",EDGE,"E25.3"),sQuery(id+"F0.wireOp",EDGE,"E25.4"),sQuery(id+"F0.wireOp",EDGE,"E25.5"),sQuery(id+"F0.wireOp",EDGE,"E25.6"),sQuery(id+"F0.wireOp",EDGE,"E25.7")])],"isStart":false});
            extrude(context, id + "F17", {"entities" : qUnion([Q0, Q1, Q2]), "endBound" : BoundingType.UP_TO_SURFACE, "depth" : 25 * mm, "endBoundEntityFace" : qUnion([Q3]), "offsetDistance" : 25 * mm});
        }
    });
